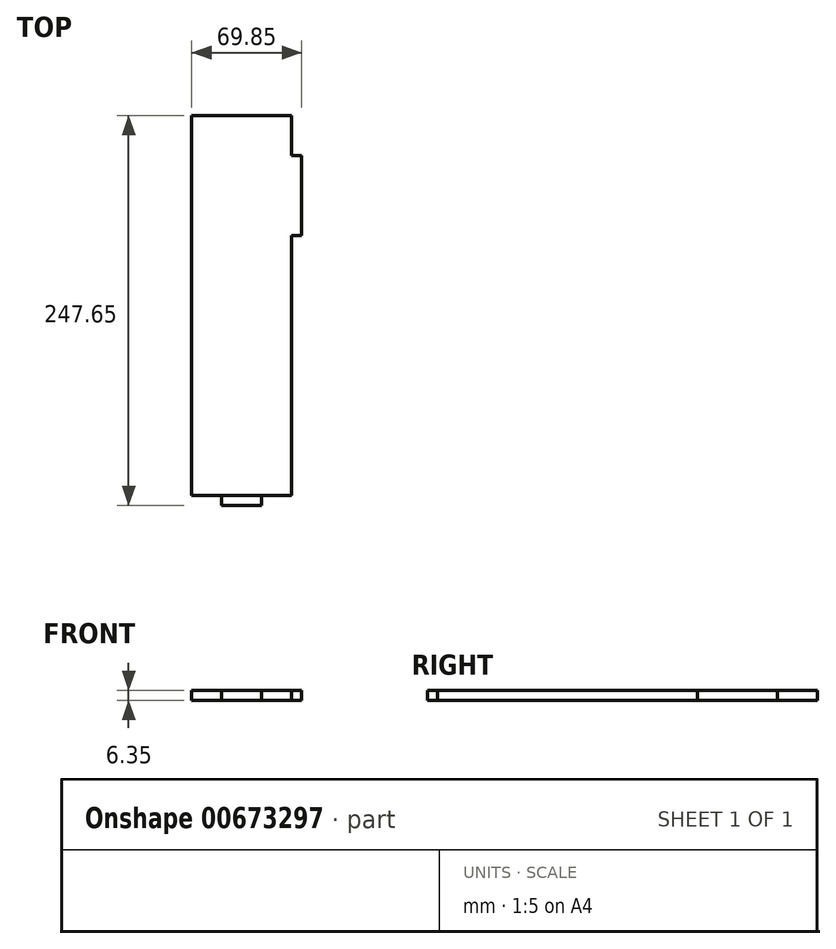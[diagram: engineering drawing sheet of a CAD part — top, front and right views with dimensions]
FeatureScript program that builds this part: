
annotation { "Feature Type Name" : "Feature", "Feature Type Description" : "" }
export const myFeature = defineFeature(function(context is Context, id is Id, definition is map)
    precondition{}
    {
        {
            var Q0;
            Q0=qCreatedBy(makeId("Top.planeOp"),FACE);
            var sketch = newSketch(context, id + "F0", { "sketchPlane" : qUnion([Q0])});
            skLineSegment(sketch, "E0.bottom", {"start": v(0, 120.65) * mm, "end": v(63.5, 120.65) * mm});
            skLineSegment(sketch, "E0.top", {"start": v(0, -120.65) * mm, "end": v(63.5, -120.65) * mm});
            skLineSegment(sketch, "E0.left", {"start": v(0, 120.65) * mm, "end": v(0, -120.65) * mm});
            skLineSegment(sketch, "E0.right", {"start": v(63.5, 120.65) * mm, "end": v(63.5, -120.65) * mm});
            skSolve(sketch);
        }
        {
            var Q0;
            Q0 = qSketchRegion(id + "F0", true);
            extrude(context, id + "F1", {"entities" : qUnion([Q0]), "depth" : 6.35 * mm, "offsetDistance" : 25.4 * mm});
        }
        {
            var Q0;
            Q0=makeQuery(id+"F1.opExtrude","CAP_FACE",FACE,{"disambiguationData":[OSD([sQuery(id+"F0.wireOp",EDGE,"E0.bottom"),sQuery(id+"F0.wireOp",EDGE,"E0.top"),sQuery(id+"F0.wireOp",EDGE,"E0.left"),sQuery(id+"F0.wireOp",EDGE,"E0.right")])],"isStart":false});
            var sketch = newSketch(context, id + "F2", { "sketchPlane" : qUnion([Q0])});
            skLineSegment(sketch, "E1.bottom", {"start": v(63.5, 95.25) * mm, "end": v(69.85, 95.25) * mm});
            skLineSegment(sketch, "E1.top", {"start": v(63.5, 44.45) * mm, "end": v(69.85, 44.45) * mm});
            skLineSegment(sketch, "E1.left", {"start": v(63.5, 95.25) * mm, "end": v(63.5, 44.45) * mm});
            skLineSegment(sketch, "E1.right", {"start": v(69.85, 95.25) * mm, "end": v(69.85, 44.45) * mm});
            skSolve(sketch);
        }
        {
            var Q0;
            Q0 = qSketchRegion(id + "F2", true);
            extrude(context, id + "F3", {"entities" : qUnion([Q0]), "operationType" : NewBodyOperationType.ADD, "oppositeDirection" : true, "depth" : 6.35 * mm, "offsetDistance" : 25.4 * mm});
        }
        {
            var Q0;
            {var subQ0=sQuery(id+"F2.wireOp",EDGE,"E1.right");var subQ1=sQuery(id+"F2.wireOp",EDGE,"E1.left");var subQ2=sQuery(id+"F2.wireOp",EDGE,"E1.top");var subQ3=sQuery(id+"F2.wireOp",EDGE,"E1.bottom");Q0=makeQuery(id+"F1vbUgS1NdXFFWh_1.1.F3.boolean.opBoolean","MERGE",FACE,{"derivedFrom":[makeQuery(id+"F3.boolean.opBoolean","MERGE",FACE,{"derivedFrom":[makeQuery(id+"F1.opExtrude","CAP_FACE",FACE,{"disambiguationData":[OSD([sQuery(id+"F0.wireOp",EDGE,"E0.bottom"),sQuery(id+"F0.wireOp",EDGE,"E0.top"),sQuery(id+"F0.wireOp",EDGE,"E0.left"),sQuery(id+"F0.wireOp",EDGE,"E0.right")])],"isStart":false}),makeQuery(id+"F3.opExtrude","CAP_FACE",FACE,{"disambiguationData":[OSD([subQ3,subQ2,subQ1,subQ0])],"isStart":true})]}),makeQuery(id+"F1vbUgS1NdXFFWh_1.1.F3.opExtrude","CAP_FACE",FACE,{"disambiguationData":[OSD([subQ3,subQ2,subQ1,subQ0])],"isStart":true})]});}
            var sketch = newSketch(context, id + "F4", { "sketchPlane" : qUnion([Q0])});
            skLineSegment(sketch, "E2.bottom", {"start": v(19.05, -120.65) * mm, "end": v(44.45, -120.65) * mm});
            skLineSegment(sketch, "E2.top", {"start": v(19.05, -127) * mm, "end": v(44.45, -127) * mm});
            skLineSegment(sketch, "E2.left", {"start": v(19.05, -127) * mm, "end": v(19.05, -120.65) * mm});
            skLineSegment(sketch, "E2.right", {"start": v(44.45, -127) * mm, "end": v(44.45, -120.65) * mm});
            skSolve(sketch);
        }
        {
            var Q0;
            Q0 = qSketchRegion(id + "F4", true);
            extrude(context, id + "F5", {"entities" : qUnion([Q0]), "oppositeDirection" : true, "depth" : 6.35 * mm, "offsetDistance" : 25.4 * mm});
        }
    });
